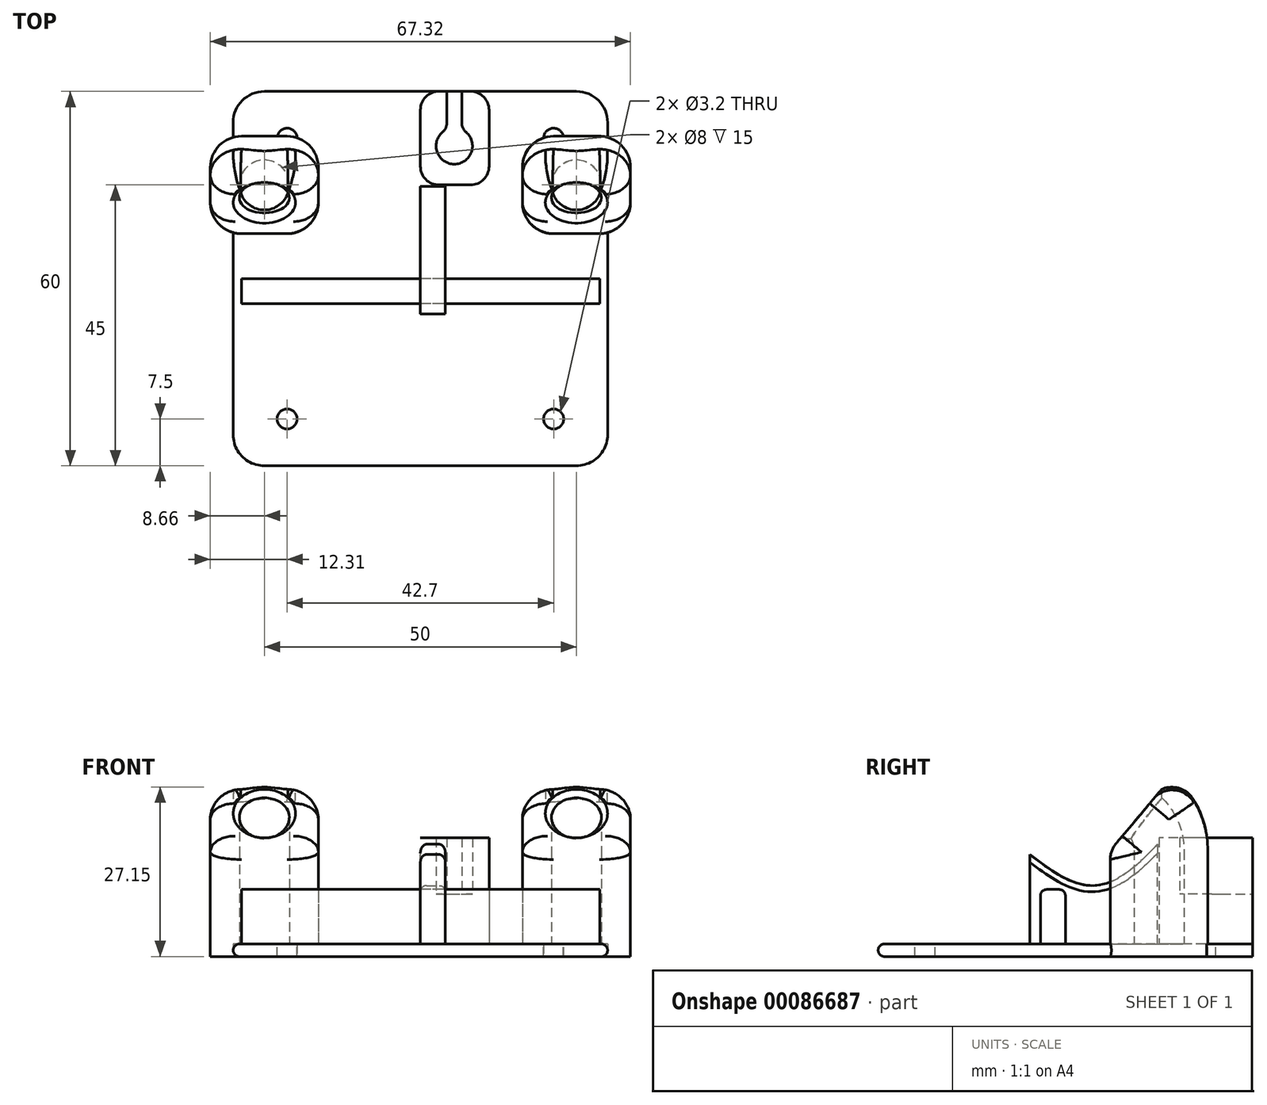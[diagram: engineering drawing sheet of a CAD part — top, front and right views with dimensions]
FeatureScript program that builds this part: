
annotation { "Feature Type Name" : "Feature", "Feature Type Description" : "" }
export const myFeature = defineFeature(function(context is Context, id is Id, definition is map)
    precondition{}
    {
        {
            var Q0;
            Q0=qCreatedBy(makeId("Top.planeOp"),FACE);
            var sketch = newSketch(context, id + "F0", { "sketchPlane" : qUnion([Q0])});
            skArc(sketch, "E0", {"start": v(25, -30) * mm, "mid": v(28.54, -28.54) * mm, "end": v(30, -25) * mm});
            skLineSegment(sketch, "E1", {"start": v(25, -30) * mm, "end": v(-25, -30) * mm});
            skArc(sketch, "E2", {"start": v(30, 25) * mm, "mid": v(28.54, 28.54) * mm, "end": v(25, 30) * mm});
            skLineSegment(sketch, "E3", {"start": v(30, 25) * mm, "end": v(30, -25) * mm});
            skArc(sketch, "E4", {"start": v(-25, 30) * mm, "mid": v(-28.54, 28.54) * mm, "end": v(-30, 25) * mm});
            skLineSegment(sketch, "E5", {"start": v(-25, 30) * mm, "end": v(25, 30) * mm});
            skArc(sketch, "E6", {"start": v(-30, -25) * mm, "mid": v(-28.54, -28.54) * mm, "end": v(-25, -30) * mm});
            skLineSegment(sketch, "E7", {"start": v(-30, -25) * mm, "end": v(-30, 25) * mm});
            skCircle(sketch, "E8", {"center": v(21.35, 22.5) * mm, "radius": 3.25 * mm});
            skCircle(sketch, "E9", {"center": v(21.35, -22.5) * mm, "radius": 3.25 * mm});
            skCircle(sketch, "E10", {"center": v(-21.35, 22.5) * mm, "radius": 3.25 * mm});
            skCircle(sketch, "E11", {"center": v(-21.35, -22.5) * mm, "radius": 3.25 * mm});
            skCircle(sketch, "E12", {"center": v(-21.35, 22.5) * mm, "radius": 4.5 * mm});
            skCircle(sketch, "E13", {"center": v(21.35, 22.5) * mm, "radius": 4.5 * mm});
            skCircle(sketch, "E14", {"center": v(21.35, -22.5) * mm, "radius": 4.5 * mm});
            skCircle(sketch, "E15", {"center": v(-21.35, -22.5) * mm, "radius": 4.5 * mm});
            skCircle(sketch, "E16", {"center": v(-21.35, 22.5) * mm, "radius": 1.6 * mm});
            skCircle(sketch, "E17", {"center": v(21.35, 22.5) * mm, "radius": 1.6 * mm});
            skCircle(sketch, "E18", {"center": v(21.35, -22.5) * mm, "radius": 1.6 * mm});
            skCircle(sketch, "E19", {"center": v(-21.35, -22.5) * mm, "radius": 1.6 * mm});
            skSolve(sketch);
        }
        {
            var Q0;
            Q0=qCreatedBy(makeId("Top.planeOp"),FACE);
            var sketch = newSketch(context, id + "F1", { "sketchPlane" : qUnion([Q0])});
            skLineSegment(sketch, "E20", {"start": v(-48.6, 15) * mm, "end": v(60.7, 15) * mm, "construction": true});
            skLineSegment(sketch, "E21", {"start": v(0, 64.77) * mm, "end": v(0, -51.05) * mm, "construction": true});
            skLineSegment(sketch, "E22", {"start": v(5.5, 55.23) * mm, "end": v(5.5, -47.1) * mm, "construction": true});
            skLineSegment(sketch, "E23", {"start": v(-25, 40.32) * mm, "end": v(-25, -3.03) * mm, "construction": true});
            skLineSegment(sketch, "E24", {"start": v(25, 40.97) * mm, "end": v(25, -7.33) * mm, "construction": true});
            skCircle(sketch, "E25", {"center": v(-25, 15) * mm, "radius": 4 * mm});
            skCircle(sketch, "E26", {"center": v(25, 15) * mm, "radius": 4 * mm});
            skCircle(sketch, "E27", {"center": v(5.5, 21.16) * mm, "radius": 2.9 * mm});
            skCircle(sketch, "E28", {"center": v(5.5, -21.16) * mm, "radius": 3.1 * mm});
            skLineSegment(sketch, "E29.bottom", {"start": v(6.7, 23.81) * mm, "end": v(4.3, 23.81) * mm});
            skLineSegment(sketch, "E29.top", {"start": v(6.7, 30.96) * mm, "end": v(4.3, 30.96) * mm});
            skLineSegment(sketch, "E29.left", {"start": v(6.7, 23.81) * mm, "end": v(6.7, 30.96) * mm});
            skLineSegment(sketch, "E29.right", {"start": v(4.3, 23.81) * mm, "end": v(4.3, 30.96) * mm});
            skPoint(sketch, "E29.middle", {"position": v(5.5, 27.39) * mm});
            skLineSegment(sketch, "E30.bottom", {"start": v(0, 30) * mm, "end": v(11, 30) * mm});
            skLineSegment(sketch, "E30.top", {"start": v(0, 15) * mm, "end": v(11, 15) * mm});
            skLineSegment(sketch, "E30.left", {"start": v(0, 30) * mm, "end": v(0, 15) * mm});
            skLineSegment(sketch, "E30.right", {"start": v(11, 30) * mm, "end": v(11, 15) * mm});
            skLineSegment(sketch, "E31.bottom", {"start": v(-28.66, 22.81) * mm, "end": v(-21.34, 22.81) * mm});
            skLineSegment(sketch, "E31.top", {"start": v(-28.66, 7.19) * mm, "end": v(-21.34, 7.19) * mm});
            skLineSegment(sketch, "E31.left", {"start": v(-33.66, 17.81) * mm, "end": v(-33.66, 12.19) * mm});
            skLineSegment(sketch, "E31.right", {"start": v(-16.34, 17.81) * mm, "end": v(-16.34, 12.19) * mm});
            skLineSegment(sketch, "E32.bottom", {"start": v(21.34, 22.81) * mm, "end": v(28.66, 22.81) * mm});
            skLineSegment(sketch, "E32.top", {"start": v(21.34, 7.19) * mm, "end": v(28.66, 7.19) * mm});
            skLineSegment(sketch, "E32.left", {"start": v(16.34, 17.81) * mm, "end": v(16.34, 12.19) * mm});
            skLineSegment(sketch, "E32.right", {"start": v(33.66, 17.81) * mm, "end": v(33.66, 12.19) * mm});
            skPoint(sketch, "E33.visualSharp", {"position": v(-33.66, 22.81) * mm});
            skArc(sketch, "E33.filletArc", {"start": v(-28.66, 22.81) * mm, "mid": v(-32.2, 21.35) * mm, "end": v(-33.66, 17.81) * mm});
            skPoint(sketch, "E34.visualSharp", {"position": v(-16.34, 22.81) * mm});
            skArc(sketch, "E34.filletArc", {"start": v(-16.34, 17.81) * mm, "mid": v(-17.8, 21.35) * mm, "end": v(-21.34, 22.81) * mm});
            skPoint(sketch, "E35.visualSharp", {"position": v(-16.34, 7.19) * mm});
            skArc(sketch, "E35.filletArc", {"start": v(-21.34, 7.19) * mm, "mid": v(-17.8, 8.65) * mm, "end": v(-16.34, 12.19) * mm});
            skPoint(sketch, "E36.visualSharp", {"position": v(-33.66, 7.19) * mm});
            skArc(sketch, "E36.filletArc", {"start": v(-33.66, 12.19) * mm, "mid": v(-32.2, 8.65) * mm, "end": v(-28.66, 7.19) * mm});
            skPoint(sketch, "E37.visualSharp", {"position": v(16.34, 22.81) * mm});
            skArc(sketch, "E37.filletArc", {"start": v(21.34, 22.81) * mm, "mid": v(17.8, 21.35) * mm, "end": v(16.34, 17.81) * mm});
            skPoint(sketch, "E38.visualSharp", {"position": v(33.66, 22.81) * mm});
            skArc(sketch, "E38.filletArc", {"start": v(33.66, 17.81) * mm, "mid": v(32.2, 21.35) * mm, "end": v(28.66, 22.81) * mm});
            skPoint(sketch, "E39.visualSharp", {"position": v(16.34, 7.19) * mm});
            skArc(sketch, "E39.filletArc", {"start": v(16.34, 12.19) * mm, "mid": v(17.8, 8.65) * mm, "end": v(21.34, 7.19) * mm});
            skPoint(sketch, "E40.visualSharp", {"position": v(33.66, 7.19) * mm});
            skArc(sketch, "E40.filletArc", {"start": v(28.66, 7.19) * mm, "mid": v(32.2, 8.65) * mm, "end": v(33.66, 12.19) * mm});
            skSolve(sketch);
        }
        {
            var Q0;
            Q0=makeQuery(id+"F1.imprint","IMPRINT",FACE,{"disambiguationData":[TD([[makeQuery(id+"F1.imprint","IMPRINT",EDGE,{"derivedFrom":sQuery(id+"F1.wireOp",EDGE,"E30.top")}),1.0]])]});
            var Q1;
            {var subQ0=sQuery(id+"F1.wireOp",EDGE,"E29.bottom");Q1=makeQuery(id+"F1.imprint","IMPRINT",FACE,{"disambiguationData":[TD([[makeQuery(id+"F1.imprint","IMPRINT",EDGE,{"derivedFrom":subQ0}),1.0]])]});}
            var Q2;
            {var subQ0=sQuery(id+"F1.wireOp",EDGE,"E29.left");var subQ6=sQuery(id+"F1.wireOp",EDGE,"E30.bottom");var subQ7=makeQuery(id+"F1.imprint","INTERSECT",VERTEX,{"derivedFrom":[subQ0,subQ6]});Q2=makeQuery(id+"F1.imprint","IMPRINT",FACE,{"disambiguationData":[TD([[makeQuery(id+"F1.imprint","IMPRINT",EDGE,{"disambiguationData":[TD([[subQ7,1.0]])],"derivedFrom":subQ6}),-1.0]])]});}
            var Q3;
            {var subQ0=sQuery(id+"F1.wireOp",EDGE,"E29.bottom");Q3=makeQuery(id+"F1.imprint","IMPRINT",FACE,{"disambiguationData":[TD([[makeQuery(id+"F1.imprint","IMPRINT",EDGE,{"derivedFrom":subQ0}),-1.0]])]});}
            extrude(context, id + "F2", {"entities" : qUnion([Q0, Q1, Q2, Q3]), "depth" : 8 * mm});
        }
        {
            var Q0;
            Q0=makeQuery(id+"F0.imprint","IMPRINT",FACE,{"disambiguationData":[TD([[makeQuery(id+"F0.imprint","IMPRINT",EDGE,{"derivedFrom":sQuery(id+"F0.wireOp",EDGE,"E0")}),1.0]])]});
            var Q1;
            Q1=makeQuery(id+"F0.imprint","IMPRINT",FACE,{"disambiguationData":[TD([[makeQuery(id+"F0.imprint","IMPRINT",EDGE,{"derivedFrom":sQuery(id+"F0.wireOp",EDGE,"E10")}),1.0]])]});
            var Q2;
            Q2=makeQuery(id+"F0.imprint","IMPRINT",FACE,{"disambiguationData":[TD([[makeQuery(id+"F0.imprint","IMPRINT",EDGE,{"derivedFrom":sQuery(id+"F0.wireOp",EDGE,"E10")}),-1.0]])]});
            var Q3;
            Q3=makeQuery(id+"F0.imprint","IMPRINT",FACE,{"disambiguationData":[TD([[makeQuery(id+"F0.imprint","IMPRINT",EDGE,{"derivedFrom":sQuery(id+"F0.wireOp",EDGE,"E8")}),1.0]])]});
            var Q4;
            Q4=makeQuery(id+"F0.imprint","IMPRINT",FACE,{"disambiguationData":[TD([[makeQuery(id+"F0.imprint","IMPRINT",EDGE,{"derivedFrom":sQuery(id+"F0.wireOp",EDGE,"E8")}),-1.0]])]});
            var Q5;
            Q5=makeQuery(id+"F0.imprint","IMPRINT",FACE,{"disambiguationData":[TD([[makeQuery(id+"F0.imprint","IMPRINT",EDGE,{"derivedFrom":sQuery(id+"F0.wireOp",EDGE,"E9")}),1.0]])]});
            var Q6;
            Q6=makeQuery(id+"F0.imprint","IMPRINT",FACE,{"disambiguationData":[TD([[makeQuery(id+"F0.imprint","IMPRINT",EDGE,{"derivedFrom":sQuery(id+"F0.wireOp",EDGE,"E9")}),-1.0]])]});
            var Q7;
            Q7=makeQuery(id+"F0.imprint","IMPRINT",FACE,{"disambiguationData":[TD([[makeQuery(id+"F0.imprint","IMPRINT",EDGE,{"derivedFrom":sQuery(id+"F0.wireOp",EDGE,"E11")}),1.0]])]});
            var Q8;
            Q8=makeQuery(id+"F0.imprint","IMPRINT",FACE,{"disambiguationData":[TD([[makeQuery(id+"F0.imprint","IMPRINT",EDGE,{"derivedFrom":sQuery(id+"F0.wireOp",EDGE,"E11")}),-1.0]])]});
            extrude(context, id + "F3", {"entities" : qUnion([Q0, Q1, Q2, Q3, Q4, Q5, Q6, Q7, Q8]), "oppositeDirection" : true, "depth" : 2 * mm});
        }
        {
            var Q0;
            Q0=makeQuery(id+"F2.opExtrude","CAP_FACE",FACE,{"disambiguationData":[OSD([sQuery(id+"F1.wireOp",EDGE,"E30.bottom"),sQuery(id+"F1.wireOp",EDGE,"E30.top"),sQuery(id+"F1.wireOp",EDGE,"E30.left"),sQuery(id+"F1.wireOp",EDGE,"E30.right")])],"isStart":false});
            var sketch = newSketch(context, id + "F4", { "sketchPlane" : qUnion([Q0])});
            skCircle(sketch, "E41", {"center": v(5.43, 21.25) * mm, "radius": 2.9 * mm});
            skLineSegment(sketch, "E42.bottom", {"start": v(6.63, 23.9) * mm, "end": v(4.23, 23.9) * mm});
            skLineSegment(sketch, "E42.top", {"start": v(6.63, 31.05) * mm, "end": v(4.23, 31.05) * mm});
            skLineSegment(sketch, "E42.left", {"start": v(6.63, 23.9) * mm, "end": v(6.63, 31.05) * mm});
            skLineSegment(sketch, "E42.right", {"start": v(4.23, 23.9) * mm, "end": v(4.23, 31.05) * mm});
            skPoint(sketch, "E42.middle", {"position": v(5.43, 27.47) * mm});
            skLineSegment(sketch, "E43.bottom", {"start": v(0, 30) * mm, "end": v(11, 30) * mm});
            skLineSegment(sketch, "E43.top", {"start": v(0, 15) * mm, "end": v(11, 15) * mm});
            skLineSegment(sketch, "E43.left", {"start": v(0, 30) * mm, "end": v(0, 15) * mm});
            skLineSegment(sketch, "E43.right", {"start": v(11, 30) * mm, "end": v(11, 15) * mm});
            skSolve(sketch);
        }
        {
            var Q0;
            {var subQ0=sQuery(id+"F4.wireOp",EDGE,"E43.right");var subQ1=sQuery(id+"F4.wireOp",EDGE,"E43.top");var subQ2=makeQuery(id+"F4.imprint","INTERSECT",VERTEX,{"derivedFrom":[subQ1,subQ0]});Q0=makeQuery(id+"F4.imprint","IMPRINT",FACE,{"disambiguationData":[TD([[makeQuery(id+"F4.imprint","IMPRINT",EDGE,{"disambiguationData":[TD([[subQ2,1.0]])],"derivedFrom":subQ1}),1.0]])]});}
            extrude(context, id + "F5", {"entities" : qUnion([Q0]), "operationType" : NewBodyOperationType.ADD, "depth" : 9 * mm});
        }
        {
            var Q0;
            Q0=makeQuery(id+"F5.opExtrude","SWEPT_EDGE",EDGE,{"disambiguationData":[OSD([sQuery(id+"F4.wireOp",EDGE,"E41"),sQuery(id+"F4.wireOp",EDGE,"E42.bottom"),sQuery(id+"F4.wireOp",EDGE,"E42.left")])]});
            var Q1;
            Q1=makeQuery(id+"F5.opExtrude","SWEPT_EDGE",EDGE,{"disambiguationData":[OSD([sQuery(id+"F4.wireOp",EDGE,"E41"),sQuery(id+"F4.wireOp",EDGE,"E42.bottom"),sQuery(id+"F4.wireOp",EDGE,"E42.right")])]});
            fillet(context, id + "F6", {"entities" : qUnion([Q0, Q1]), "radius" : 2 * mm, "tangentPropagation" : true, "allowEdgeOverflow" : false});
        }
        {
            var Q0;
            Q0=qCreatedBy(makeId("Right.planeOp"),FACE);
            var sketch = newSketch(context, id + "F7", { "sketchPlane" : qUnion([Q0])});
            skFitSpline(sketch, "E44", {"points": [v(14.76, 16) * mm, v(-5.68, 14.35) * mm], "startDerivative": vector(-24.35, -26.04) * mm, "endDerivative": vector(-25.64, 20.3) * mm});
            skLineSegment(sketch, "E45", {"start": v(-5.68, 14.35) * mm, "end": v(-5.68, 0) * mm});
            skLineSegment(sketch, "E46", {"start": v(-5.68, 0) * mm, "end": v(14.76, 0) * mm});
            skLineSegment(sketch, "E47", {"start": v(14.76, 0) * mm, "end": v(14.76, 16) * mm});
            skSolve(sketch);
        }
        {
            var Q0;
            Q0 = qSketchRegion(id + "F7", true);
            extrude(context, id + "F8", {"entities" : qUnion([Q0]), "depth" : 4 * mm});
        }
        {
            var Q0;
            Q0=makeQuery(id+"F5.boolean.opBoolean","MERGE",EDGE,{"derivedFrom":[makeQuery(id+"F2.opExtrude","SWEPT_EDGE",EDGE,{"disambiguationData":[OSD([sQuery(id+"F1.wireOp",EDGE,"E30.top"),sQuery(id+"F1.wireOp",EDGE,"E30.right")])]}),makeQuery(id+"F5.opExtrude","SWEPT_EDGE",EDGE,{"disambiguationData":[OSD([sQuery(id+"F4.wireOp",EDGE,"E43.top"),sQuery(id+"F4.wireOp",EDGE,"E43.right")])]})]});
            var Q1;
            Q1=makeQuery(id+"F5.boolean.opBoolean","MERGE",EDGE,{"derivedFrom":[makeQuery(id+"F2.opExtrude","SWEPT_EDGE",EDGE,{"disambiguationData":[OSD([sQuery(id+"F1.wireOp",EDGE,"E30.bottom"),sQuery(id+"F1.wireOp",EDGE,"E30.right")])]}),makeQuery(id+"F5.opExtrude","SWEPT_EDGE",EDGE,{"disambiguationData":[OSD([sQuery(id+"F4.wireOp",EDGE,"E43.bottom"),sQuery(id+"F4.wireOp",EDGE,"E43.right")])]})]});
            var Q2;
            Q2=makeQuery(id+"F5.boolean.opBoolean","MERGE",EDGE,{"derivedFrom":[makeQuery(id+"F2.opExtrude","SWEPT_EDGE",EDGE,{"disambiguationData":[OSD([sQuery(id+"F1.wireOp",EDGE,"E30.bottom"),sQuery(id+"F1.wireOp",EDGE,"E30.left")])]}),makeQuery(id+"F5.opExtrude","SWEPT_EDGE",EDGE,{"disambiguationData":[OSD([sQuery(id+"F4.wireOp",EDGE,"E43.bottom"),sQuery(id+"F4.wireOp",EDGE,"E43.left")])]})]});
            var Q3;
            Q3=makeQuery(id+"F5.boolean.opBoolean","MERGE",EDGE,{"derivedFrom":[makeQuery(id+"F2.opExtrude","SWEPT_EDGE",EDGE,{"disambiguationData":[OSD([sQuery(id+"F1.wireOp",EDGE,"E30.top"),sQuery(id+"F1.wireOp",EDGE,"E30.left")])]}),makeQuery(id+"F5.opExtrude","SWEPT_EDGE",EDGE,{"disambiguationData":[OSD([sQuery(id+"F4.wireOp",EDGE,"E43.top"),sQuery(id+"F4.wireOp",EDGE,"E43.left")])]})]});
            fillet(context, id + "F9", {"entities" : qUnion([Q0, Q1, Q2, Q3]), "radius" : 3 * mm, "tangentPropagation" : true, "allowEdgeOverflow" : false});
        }
        {
            var Q0;
            Q0=makeQuery(id+"F1.imprint","IMPRINT",FACE,{"disambiguationData":[TD([[makeQuery(id+"F1.imprint","IMPRINT",EDGE,{"derivedFrom":sQuery(id+"F1.wireOp",EDGE,"E25")}),-1.0]])]});
            var Q1;
            Q1=makeQuery(id+"F1.imprint","IMPRINT",FACE,{"disambiguationData":[TD([[makeQuery(id+"F1.imprint","IMPRINT",EDGE,{"derivedFrom":sQuery(id+"F1.wireOp",EDGE,"E26")}),-1.0]])]});
            extrude(context, id + "F10", {"entities" : qUnion([Q0, Q1]), "depth" : 15 * mm});
        }
        {
            var Q0;
            Q0=makeQuery(id+"F10.opExtrude","CAP_FACE",FACE,{"disambiguationData":[OSD([sQuery(id+"F1.wireOp",EDGE,"E25"),sQuery(id+"F1.wireOp",EDGE,"E31.bottom"),sQuery(id+"F1.wireOp",EDGE,"E31.top"),sQuery(id+"F1.wireOp",EDGE,"E31.left"),sQuery(id+"F1.wireOp",EDGE,"E31.right"),sQuery(id+"F1.wireOp",EDGE,"E33.filletArc"),sQuery(id+"F1.wireOp",EDGE,"E34.filletArc"),sQuery(id+"F1.wireOp",EDGE,"E35.filletArc"),sQuery(id+"F1.wireOp",EDGE,"E36.filletArc")])],"isStart":false});
            var Q1;
            Q1=makeQuery(id+"F10.opExtrude","CAP_FACE",FACE,{"disambiguationData":[OSD([sQuery(id+"F1.wireOp",EDGE,"E26"),sQuery(id+"F1.wireOp",EDGE,"E32.bottom"),sQuery(id+"F1.wireOp",EDGE,"E32.top"),sQuery(id+"F1.wireOp",EDGE,"E32.left"),sQuery(id+"F1.wireOp",EDGE,"E32.right"),sQuery(id+"F1.wireOp",EDGE,"E37.filletArc"),sQuery(id+"F1.wireOp",EDGE,"E38.filletArc"),sQuery(id+"F1.wireOp",EDGE,"E39.filletArc"),sQuery(id+"F1.wireOp",EDGE,"E40.filletArc")])],"isStart":false});
            var Q2;
            Q2=makeQuery(id+"F10.opExtrude","CAP_EDGE",EDGE,{"disambiguationData":[OSD([sQuery(id+"F1.wireOp",EDGE,"E31.top")])],"isStart":false});
            revolve(context, id + "F11", {"operationType" : NewBodyOperationType.ADD, "entities" : qUnion([Q0, Q1]), "axis" : qUnion([Q2]), "revolveType" : RevolveType.ONE_DIRECTION, "angle" : 50 * degree});
        }
        {
            var Q0;
            Q0=makeQuery(id+"F11.opRevolve","CAP_EDGE",EDGE,{"disambiguationData":[OSD([sQuery(id+"F1.wireOp",EDGE,"E25")])],"isStart":false});
            var Q1;
            Q1=makeQuery(id+"F11.opRevolve","CAP_EDGE",EDGE,{"disambiguationData":[OSD([sQuery(id+"F1.wireOp",EDGE,"E26")])],"isStart":false});
            chamfer(context, id + "F12", {"entities" : qUnion([Q0, Q1]), "width" : 1 * mm, "tangentPropagation" : true});
        }
        {
            var Q0;
            Q0=makeQuery(id+"F11.opRevolve","CAP_EDGE",EDGE,{"disambiguationData":[OSD([sQuery(id+"F1.wireOp",EDGE,"E31.bottom")])],"isStart":false});
            var Q1;
            Q1=makeQuery(id+"F11.opRevolve","CAP_EDGE",EDGE,{"disambiguationData":[OSD([sQuery(id+"F1.wireOp",EDGE,"E32.bottom")])],"isStart":false});
            fillet(context, id + "F13", {"entities" : qUnion([Q0, Q1]), "radius" : 4 * mm, "tangentPropagation" : true, "allowEdgeOverflow" : false});
        }
        {
            var Q0;
            Q0=qCreatedBy(makeId("Front.planeOp"),FACE);
            var sketch = newSketch(context, id + "F14", { "sketchPlane" : qUnion([Q0])});
            skLineSegment(sketch, "E48.bottom", {"start": v(28.74, 0) * mm, "end": v(-28.68, 0) * mm});
            skLineSegment(sketch, "E48.top", {"start": v(28.74, 8.74) * mm, "end": v(-28.68, 8.74) * mm});
            skLineSegment(sketch, "E48.left", {"start": v(28.74, 0) * mm, "end": v(28.74, 8.74) * mm});
            skLineSegment(sketch, "E48.right", {"start": v(-28.68, 0) * mm, "end": v(-28.68, 8.74) * mm});
            skSolve(sketch);
        }
        {
            var Q0;
            Q0 = qSketchRegion(id + "F14", true);
            extrude(context, id + "F15", {"entities" : qUnion([Q0]), "depth" : 4 * mm});
        }
        {
            var Q0;
            Q0=makeQuery(id+"F10.opExtrude","CAP_FACE",FACE,{"disambiguationData":[OSD([sQuery(id+"F1.wireOp",EDGE,"E26"),sQuery(id+"F1.wireOp",EDGE,"E32.bottom"),sQuery(id+"F1.wireOp",EDGE,"E32.top"),sQuery(id+"F1.wireOp",EDGE,"E32.left"),sQuery(id+"F1.wireOp",EDGE,"E32.right"),sQuery(id+"F1.wireOp",EDGE,"E37.filletArc"),sQuery(id+"F1.wireOp",EDGE,"E38.filletArc"),sQuery(id+"F1.wireOp",EDGE,"E39.filletArc"),sQuery(id+"F1.wireOp",EDGE,"E40.filletArc")])],"isStart":true});
            var Q1;
            Q1=makeQuery(id+"F10.opExtrude","CAP_FACE",FACE,{"disambiguationData":[OSD([sQuery(id+"F1.wireOp",EDGE,"E25"),sQuery(id+"F1.wireOp",EDGE,"E31.bottom"),sQuery(id+"F1.wireOp",EDGE,"E31.top"),sQuery(id+"F1.wireOp",EDGE,"E31.left"),sQuery(id+"F1.wireOp",EDGE,"E31.right"),sQuery(id+"F1.wireOp",EDGE,"E33.filletArc"),sQuery(id+"F1.wireOp",EDGE,"E34.filletArc"),sQuery(id+"F1.wireOp",EDGE,"E35.filletArc"),sQuery(id+"F1.wireOp",EDGE,"E36.filletArc")])],"isStart":true});
            extrude(context, id + "F16", {"entities" : qUnion([Q0, Q1]), "operationType" : NewBodyOperationType.ADD, "depth" : 2 * mm});
        }
        {
            var Q0;
            Q0=makeQuery(id+"F15.opExtrude","CAP_EDGE",EDGE,{"disambiguationData":[OSD([sQuery(id+"F14.wireOp",EDGE,"E48.top")])],"isStart":true});
            var Q1;
            Q1=makeQuery(id+"F15.opExtrude","CAP_EDGE",EDGE,{"disambiguationData":[OSD([sQuery(id+"F14.wireOp",EDGE,"E48.top")])],"isStart":false});
            var Q2;
            Q2=makeQuery(id+"F8.opExtrude","CAP_EDGE",EDGE,{"disambiguationData":[OSD([sQuery(id+"F7.wireOp",EDGE,"E44")])],"isStart":true});
            var Q3;
            Q3=makeQuery(id+"F8.opExtrude","CAP_EDGE",EDGE,{"disambiguationData":[OSD([sQuery(id+"F7.wireOp",EDGE,"E44")])],"isStart":false});
            fillet(context, id + "F17", {"entities" : qUnion([Q0, Q1, Q2, Q3]), "radius" : 1 * mm, "tangentPropagation" : true, "allowEdgeOverflow" : false});
        }
        {
            var Q0;
            Q0=makeQuery(id+"F3.opExtrude","CAP_EDGE",EDGE,{"disambiguationData":[OSD([sQuery(id+"F0.wireOp",EDGE,"E1")])],"isStart":true});
            var Q1;
            Q1=makeQuery(id+"F3.opExtrude","CAP_EDGE",EDGE,{"disambiguationData":[OSD([sQuery(id+"F0.wireOp",EDGE,"E1")])],"isStart":false});
            fillet(context, id + "F18", {"entities" : qUnion([Q0, Q1]), "radius" : 1 * mm, "tangentPropagation" : true, "allowEdgeOverflow" : false});
        }
    });
